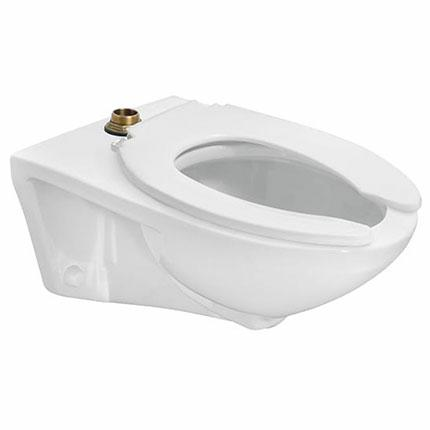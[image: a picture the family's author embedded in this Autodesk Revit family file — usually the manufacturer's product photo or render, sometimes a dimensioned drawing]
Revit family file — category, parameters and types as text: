
# Revit family: TZF NAO PARED
name_source: partatom
category: Plumbing Fixtures
units: mm (PartAtom-declared; Revit-internal decimal feet)

## family parameters
Always vertical = Yes
Cut with Voids When Loaded = No
OmniClass Number = 23.45.05.14.31
OmniClass Title = Combination Toilets
Part Type = Normal
Room Calculation Point = Yes
Round Connector Dimension = Use Diameter
Shared = Yes
Work Plane-Based = Yes

## types (2) — shared parameters
CW Connection = Yes
Default Elevation = 0"
Inlet Threads = Feeding: 15/16" - 14 NS-1; Flush: Coupled With Sanitary Flange
Manufacturer = HELVEX S.A. de C.V.
Material = High Gloss Ceramic
Max. Working Pressure = 85.3 psi
Total Length = 26"
Type Comments = Flush Toilet
Waste Connection = Yes

## per-type parameters (varying)
| type | Certification | Compliance | Description | Documentation | Features | Instructive | Min. Working Pressure | Total Height | Total Width | Type Image | URL |
| TZF NAO | http://www.helvex.com.mx | NOM-009-CONAGUA-1996 | 1.26 gpf Nao Flush Toilet With Exposed Trapway | http://www.helvex.com.mx | Requires 1.26 gpf Flush Valve; Sleek Ergonomic Design; Siphon Action Jetted Bowl; Flat Base; Sturdy Built; Optimum Water Surface; Maximum Efficiency; Saves On Water Consumption | http://www.helvex.com.mx | 14.2 psi | 15" | 15" | <None> | http://www.helvex.com.mx |
| TZF NAO PARED | https://www.helvex.com.mx | a NOM-009-CONAGUA-2001
y NOM-010-CONAGUA-2000. | Inodoro para Fluxometro, Elongado a Pared, Trampa
Oculta, 6 l, Ecolygico 3.5 / 4.8 l | https://www.helvex.com.mx | Disexo ergonymico
Mixima eficiencia en descarga
Mueble libre de alabeo (base plana)
Cerimica porcelanizada de alto brillo
Calidad (A)
Descarga tipo vyrtice con sifyn jet
Espejo de agua optimo | https://www.helvex.com.mx | 19.9 psi | 14" | 16" | TZF NAO PARED.jpg | https://www.helvex.com.mx |

note: column(s) folded — value = type name in every type: Model

## geometry (parser evidence)
native form markers: Blend x4, Sweep x2
no freeform markers — native parametric forms only
